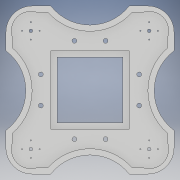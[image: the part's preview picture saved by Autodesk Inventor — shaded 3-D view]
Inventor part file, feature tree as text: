
AUTODESK INVENTOR PART (.ipt)
format: ipt  version: 2019 (Build 230136000, 136)  size: 343,552 bytes
history: native  units: mm
features: extrude x7, sketch x7, other x1, shell x1
ambient origin geometry x8: Origin, YZ Plane, XZ Plane, XY Plane, X Axis, Y Axis, Z Axis, Center Point
bodies: Body1 (feature_tree)
feature tree (16):
  other  "Твердое тело1"
  extrude  "Выдавливание1"  Depth=135.0mm
  extrude  "Выдавливание2"  Depth=135.0mm
  extrude  "Выдавливание3"  Depth=20.0mm
  extrude  "Выдавливание4"  Depth=20.0mm
  shell  "Оболочка1"  Thickness=20.0mm
  sketch  "Эскиз5"
  extrude  "Выдавливание6"  Depth=20.0mm
  extrude  "Выдавливание7"  Depth=21.5mm
  extrude  "Выдавливание8"  Depth=21.5mm
  sketch  "Эскиз1"
  sketch  "Эскиз2"
  sketch  "Эскиз3"
  sketch  "Эскиз4"
  sketch  "Эскиз6"
  sketch  "Эскиз7"
